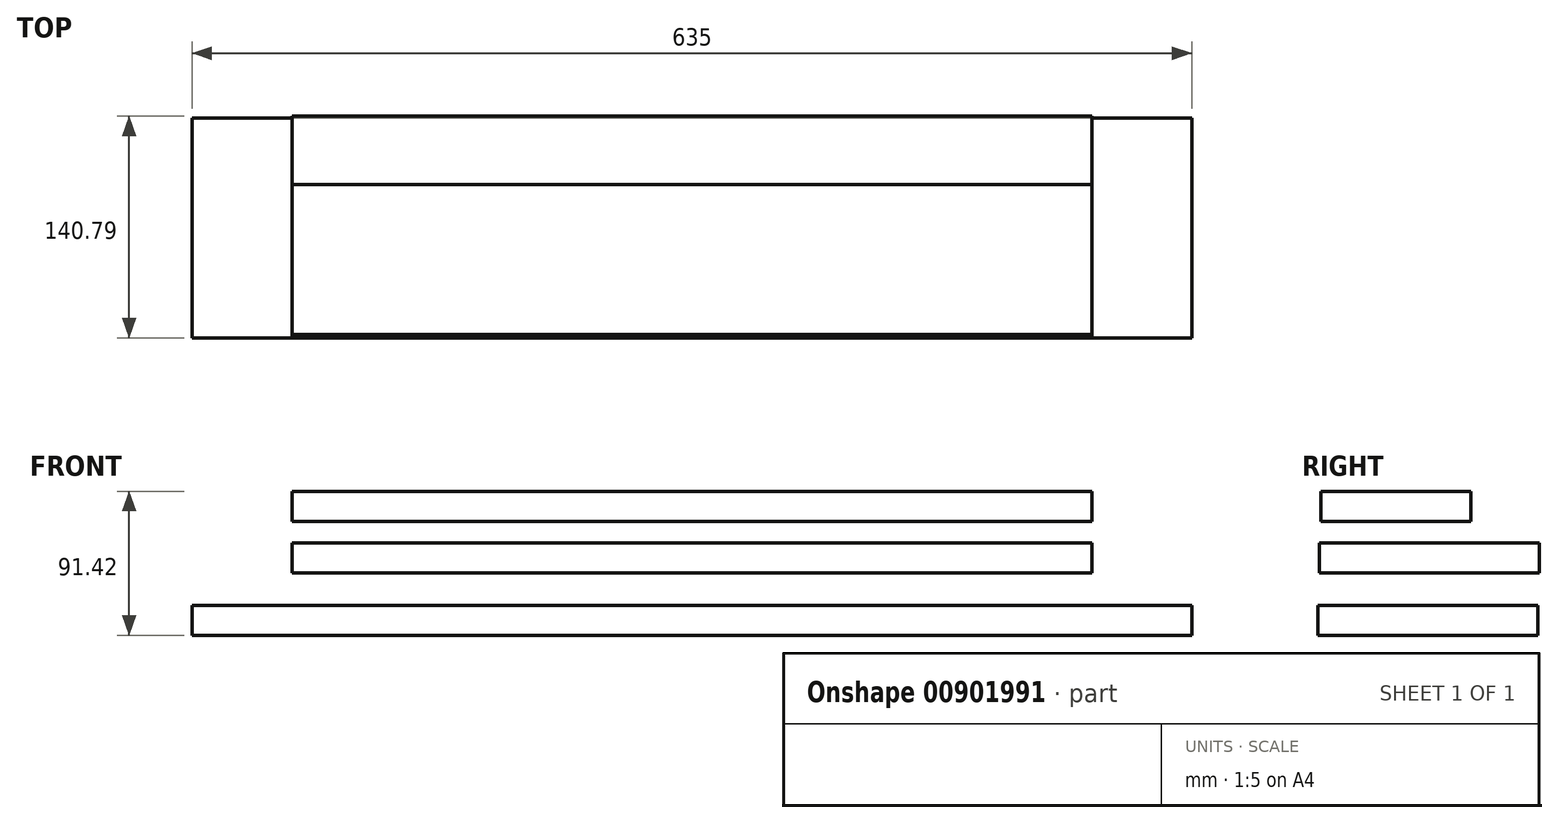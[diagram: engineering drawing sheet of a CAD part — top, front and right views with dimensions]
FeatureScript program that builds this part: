
annotation { "Feature Type Name" : "Feature", "Feature Type Description" : "" }
export const myFeature = defineFeature(function(context is Context, id is Id, definition is map)
    precondition{}
    {
        {
            var Q0;
            Q0=qCreatedBy(makeId("Right.planeOp"),FACE);
            var sketch = newSketch(context, id + "F0", { "sketchPlane" : qUnion([Q0])});
            skLineSegment(sketch, "E0.bottom", {"start": v(-70.35, 71.29) * mm, "end": v(24.9, 71.29) * mm});
            skLineSegment(sketch, "E0.top", {"start": v(-70.35, 52.24) * mm, "end": v(24.9, 52.24) * mm});
            skLineSegment(sketch, "E0.left", {"start": v(-70.35, 71.29) * mm, "end": v(-70.35, 52.24) * mm});
            skLineSegment(sketch, "E0.right", {"start": v(24.9, 71.29) * mm, "end": v(24.9, 52.24) * mm});
            skSolve(sketch);
        }
        {
            var Q0;
            Q0 = qSketchRegion(id + "F0", true);
            extrude(context, id + "F1", {"entities" : qUnion([Q0]), "endBound" : BoundingType.SYMMETRIC, "depth" : 508 * mm, "offsetDistance" : 25.4 * mm});
        }
        {
            var Q0;
            Q0=qCreatedBy(makeId("Right.planeOp"),FACE);
            var sketch = newSketch(context, id + "F2", { "sketchPlane" : qUnion([Q0])});
            skLineSegment(sketch, "E1.bottom", {"start": v(-71.32, 38.5) * mm, "end": v(68.38, 38.5) * mm});
            skLineSegment(sketch, "E1.top", {"start": v(-71.32, 19.45) * mm, "end": v(68.38, 19.45) * mm});
            skLineSegment(sketch, "E1.left", {"start": v(-71.32, 38.5) * mm, "end": v(-71.32, 19.45) * mm});
            skLineSegment(sketch, "E1.right", {"start": v(68.38, 38.5) * mm, "end": v(68.38, 19.45) * mm});
            skSolve(sketch);
        }
        {
            var Q0;
            Q0 = qSketchRegion(id + "F2", true);
            extrude(context, id + "F3", {"entities" : qUnion([Q0]), "endBound" : BoundingType.SYMMETRIC, "depth" : 508 * mm, "offsetDistance" : 25.4 * mm});
        }
        {
            var Q0;
            Q0=qCreatedBy(makeId("Right.planeOp"),FACE);
            var sketch = newSketch(context, id + "F4", { "sketchPlane" : qUnion([Q0])});
            skLineSegment(sketch, "E2.bottom", {"start": v(-72.41, -1.08) * mm, "end": v(67.29, -1.08) * mm});
            skLineSegment(sketch, "E2.top", {"start": v(-72.41, -20.13) * mm, "end": v(67.29, -20.13) * mm});
            skLineSegment(sketch, "E2.left", {"start": v(-72.41, -1.08) * mm, "end": v(-72.41, -20.13) * mm});
            skLineSegment(sketch, "E2.right", {"start": v(67.29, -1.08) * mm, "end": v(67.29, -20.13) * mm});
            skSolve(sketch);
        }
        {
            var Q0;
            Q0 = qSketchRegion(id + "F4", true);
            extrude(context, id + "F5", {"entities" : qUnion([Q0]), "endBound" : BoundingType.SYMMETRIC, "depth" : 635 * mm, "offsetDistance" : 25.4 * mm});
        }
    });
